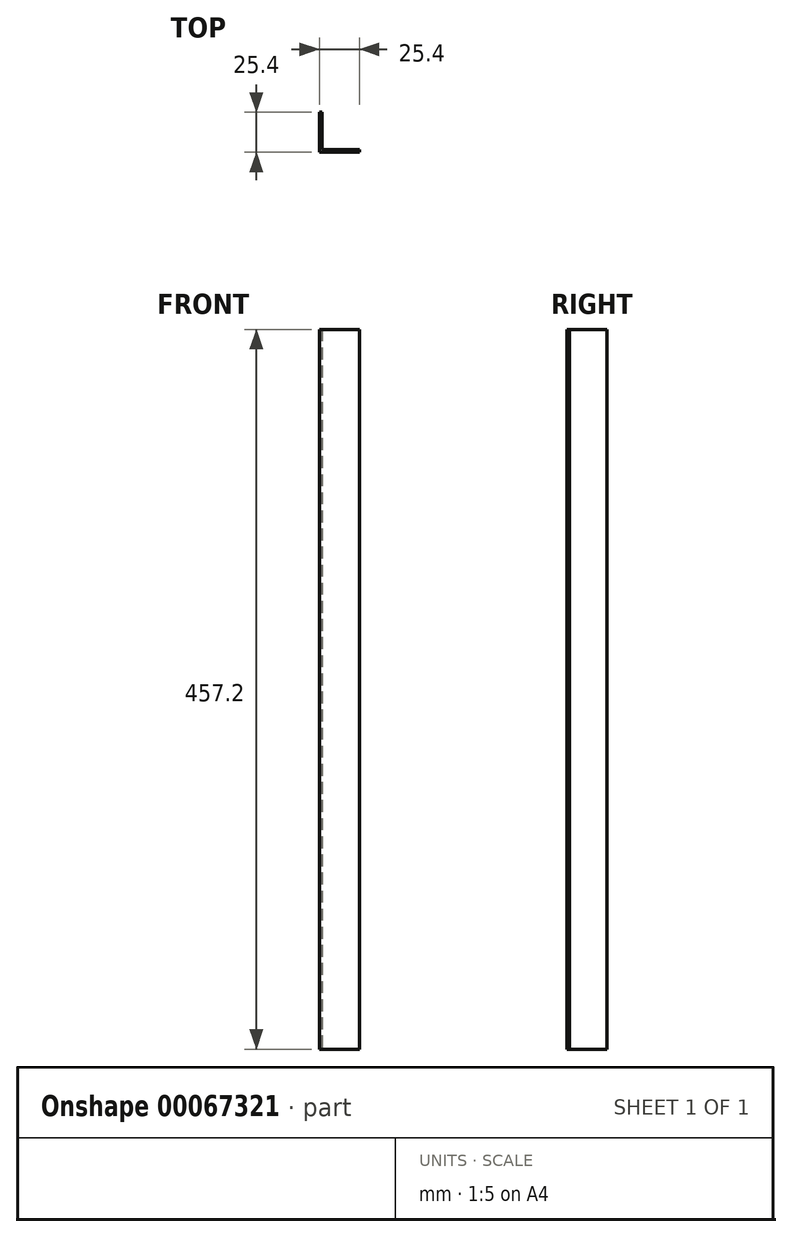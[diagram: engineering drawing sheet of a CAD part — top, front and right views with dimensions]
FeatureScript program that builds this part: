
annotation { "Feature Type Name" : "Feature", "Feature Type Description" : "" }
export const myFeature = defineFeature(function(context is Context, id is Id, definition is map)
    precondition{}
    {
        {
            var Q0;
            Q0=qCreatedBy(makeId("Top.planeOp"),FACE);
            var sketch = newSketch(context, id + "F0", { "sketchPlane" : qUnion([Q0])});
            skLineSegment(sketch, "E0", {"start": v(-3.8, 8.18) * mm, "end": v(-3.8, -17.22) * mm});
            skLineSegment(sketch, "E1", {"start": v(-3.8, -17.22) * mm, "end": v(21.6, -17.22) * mm});
            skLineSegment(sketch, "E2", {"start": v(21.6, -17.22) * mm, "end": v(21.6, -15.63) * mm});
            skLineSegment(sketch, "E3", {"start": v(21.6, -15.63) * mm, "end": v(-2.22, -15.63) * mm});
            skLineSegment(sketch, "E4", {"start": v(-2.22, -15.63) * mm, "end": v(-2.22, 8.18) * mm});
            skLineSegment(sketch, "E5", {"start": v(-2.22, 8.18) * mm, "end": v(-3.8, 8.18) * mm});
            skSolve(sketch);
        }
        {
            var Q0;
            Q0=makeQuery(id+"F0.imprint","IMPRINT",FACE,{"disambiguationData":[TD([[makeQuery(id+"F0.imprint","IMPRINT",EDGE,{"derivedFrom":sQuery(id+"F0.wireOp",EDGE,"E0")}),1.0]])]});
            extrude(context, id + "F1", {"entities" : qUnion([Q0]), "depth" : 457.2 * mm});
        }
    });
